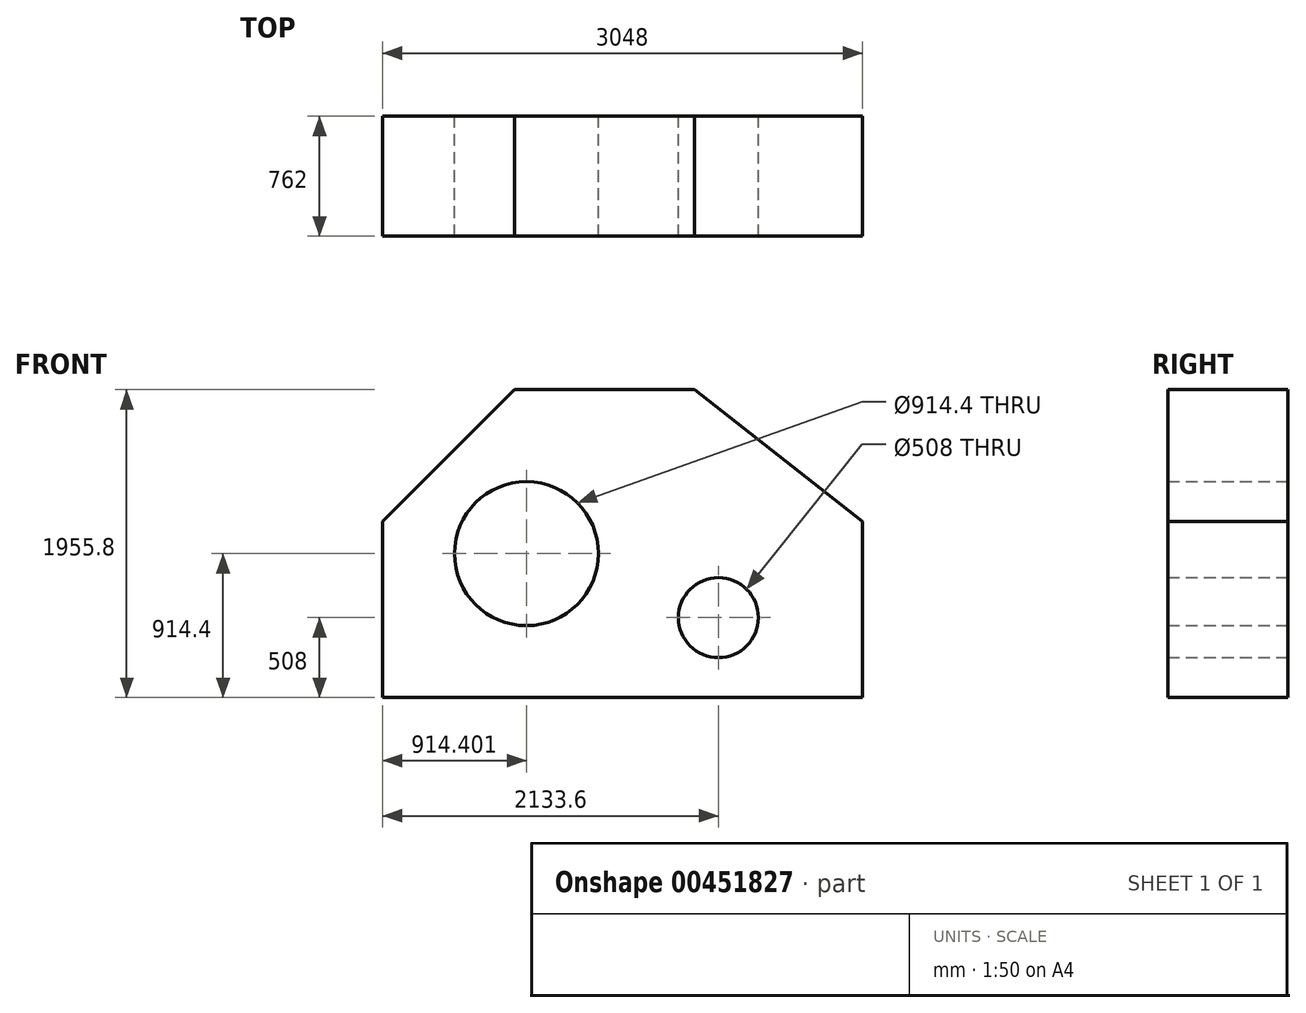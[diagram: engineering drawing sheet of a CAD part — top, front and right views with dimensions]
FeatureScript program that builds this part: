
annotation { "Feature Type Name" : "Feature", "Feature Type Description" : "" }
export const myFeature = defineFeature(function(context is Context, id is Id, definition is map)
    precondition{}
    {
        {
            var Q0;
            Q0=qCreatedBy(makeId("Front.planeOp"),FACE);
            var sketch = newSketch(context, id + "F0", { "sketchPlane" : qUnion([Q0])});
            skLineSegment(sketch, "E0", {"start": v(1464.55, 0) * mm, "end": v(-1583.45, 0) * mm});
            skLineSegment(sketch, "E1", {"start": v(-1583.45, 0) * mm, "end": v(-1583.45, 1117.6) * mm});
            skLineSegment(sketch, "E2", {"start": v(-1583.45, 1117.6) * mm, "end": v(-745.25, 1955.8) * mm});
            skLineSegment(sketch, "E3", {"start": v(-745.25, 1955.8) * mm, "end": v(397.75, 1955.8) * mm});
            skLineSegment(sketch, "E4", {"start": v(397.75, 1955.8) * mm, "end": v(1464.55, 1117.6) * mm});
            skLineSegment(sketch, "E5", {"start": v(1464.55, 1117.6) * mm, "end": v(1464.55, 0) * mm});
            skPoint(sketch, "E6.orphan", {"position": v(1616.26, 0) * mm});
            skCircle(sketch, "E7", {"center": v(-669.05, 914.4) * mm, "radius": 457.2 * mm});
            skCircle(sketch, "E8", {"center": v(550.15, 508) * mm, "radius": 254 * mm});
            skSolve(sketch);
        }
        {
            var Q0;
            Q0=makeQuery(id+"F0.imprint","IMPRINT",FACE,{"disambiguationData":[TD([[makeQuery(id+"F0.imprint","IMPRINT",EDGE,{"derivedFrom":sQuery(id+"F0.wireOp",EDGE,"E0")}),-1.0]])]});
            extrude(context, id + "F1", {"entities" : qUnion([Q0]), "depth" : 762 * mm});
        }
    });
